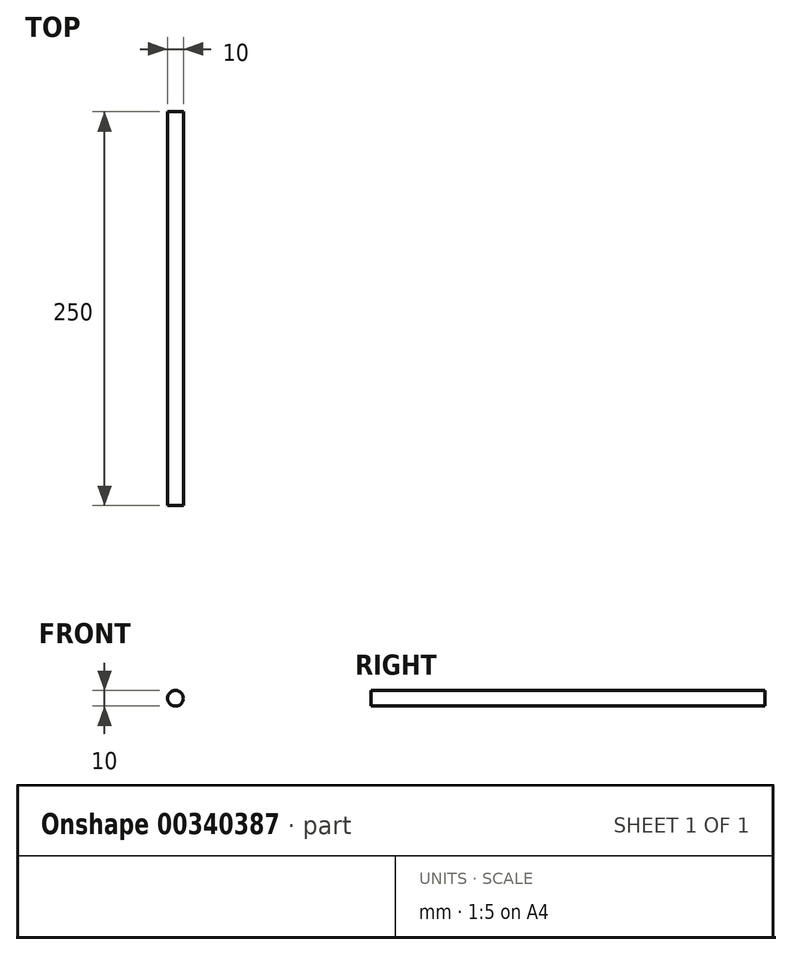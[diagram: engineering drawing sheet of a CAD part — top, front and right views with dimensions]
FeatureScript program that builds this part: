
annotation { "Feature Type Name" : "Feature", "Feature Type Description" : "" }
export const myFeature = defineFeature(function(context is Context, id is Id, definition is map)
    precondition{}
    {
        {
            var Q0;
            Q0=qCreatedBy(makeId("Front.planeOp"),FACE);
            var sketch = newSketch(context, id + "F0", { "sketchPlane" : qUnion([Q0])});
            skCircle(sketch, "E0", {"center": v(0, 0) * mm, "radius": 5 * mm});
            skSolve(sketch);
        }
        {
            var Q0;
            Q0 = qSketchRegion(id + "F0", true);
            extrude(context, id + "F1", {"entities" : qUnion([Q0]), "depth" : 250 * mm});
        }
    });
